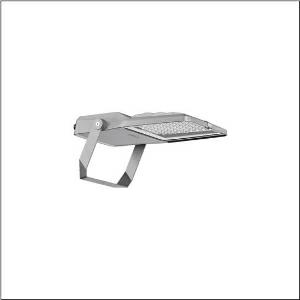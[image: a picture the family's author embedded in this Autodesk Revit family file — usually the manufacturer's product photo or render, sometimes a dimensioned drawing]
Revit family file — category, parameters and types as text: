
# Revit family: floodlight_fl_21_mini___pl52_5xa7775b2d1a_29c3
name_source: partatom
category: Lighting Fixtures
units: mm (PartAtom-declared; Revit-internal decimal feet)

## family parameters
Cut with Voids When Loaded = No
Host = Face
Light Source = No
Part Type = Normal
Room Calculation Point = No
Round Connector Dimension = Use Diameter
Shared = No

## types (1)
- --- (1 x LED, 6230 lm, 45.7 W, 3000K)
    Apparent Load = 46 VA
    CIE Flux Codes = 26 60 98 100 100
    Color Rendering = 70
    Color Temperature = 3000K
    Default Elevation = 1800 mm
    Description = Floodlight FL 21 mini, floodlight, primary light control with lens, of PMMA, primary optical cover: protective disc, of toughened safety glass, transparent, light distribution: PL52, light emission: direct distribution, installation type: surface-mounted, LED, High Power LED, rated luminous flux: 6.230lm, luminous efficacy: 136lm/W, light colour: 730, colour temperature: 3000K, control gear: Smart Interface (Zhaga), control: flexible luminous flux parameterisation, time-dependent luminous flux control, constant luminous flux control, overheat protection, pre-setting: logarithmic dimming characteristic, with terminal, 6-pole, mains connection: 220..240V, AC, 50/60Hz, start of lifetime: 46W, end of service life: 48W, reduction: 22W, luminaire housing, of diecast aluminium, powder-coated, Siteco® metallic grey (DB 702S), corrosivity category C5 mid according to DIN EN ISO 12944, suitable for swimming pools, chlorine-resistant, sealing non-destructively replaceable, mounting bracket, of steel, galvanised, powder-coated, Siteco® metallic grey (DB 702S), Smart Interface above, protection rating (complete): IP66, insulation class (complete): insulation class II (safety insulation), certification: CE, ENEC, VDE, protection symbol: D, impact resistance: IK08, permissible operating ambient temperature: -40..+40°C, permissible operating ambient temperature for outdoor applications: -40..+50°C, standard: DIN EN 12944, LABS conformity tested according to VDMA 24364:2018-05, packaging unit: 1 piece

Light Distribution: PL52
    Height = 70 mm
    Lamp = 1 x LED
    Lamp Light Flux = 6230 lm
    Lamp Power = 45.7 W
    Lamp count = 1
    Length = 485 mm
    Luminous efficacy = 136 lm/W
    Manufacturer = Siteco
    ModVariant = No
    Model = 5XA7775B2D1A
    Number of Poles = 1
    OnlyDefault = Yes
    Power Factor = 1
    Product Name = Floodlight FL 21 mini | PL52
    Product group = floodlight | pylon annexe
    ProductGroupID = 6200
    Protection Class = Protection class II
    Protection Degree = IP 66
    RLX_Detail_Level = 1
    RLX_Emergency_Light_Flux = 0 lm
    RLX_Emergency_Type = 0
    RLX_Emergency_Type_DB = No
    RlxData = <blob elided: 96241 chars, md5=8e8b0f51>
    Socket = socket
    Standby Power = 0 W
    System Light Flux = 6230 lm
    System Power = 46 W
    Type Comments = factory setting: luminous flux: 100 % | dim-lin: 254 | 463 mA
    Type Image = l_1006845.jpg
    URL = http://relux.com
    VarID = @adj_163488
    Voltage = 0 V
    Weight = 0.00 kg
    Width = 337 mm

## geometry (parser evidence)
native form markers: Blend x4, Sweep x14
no freeform markers — native parametric forms only
